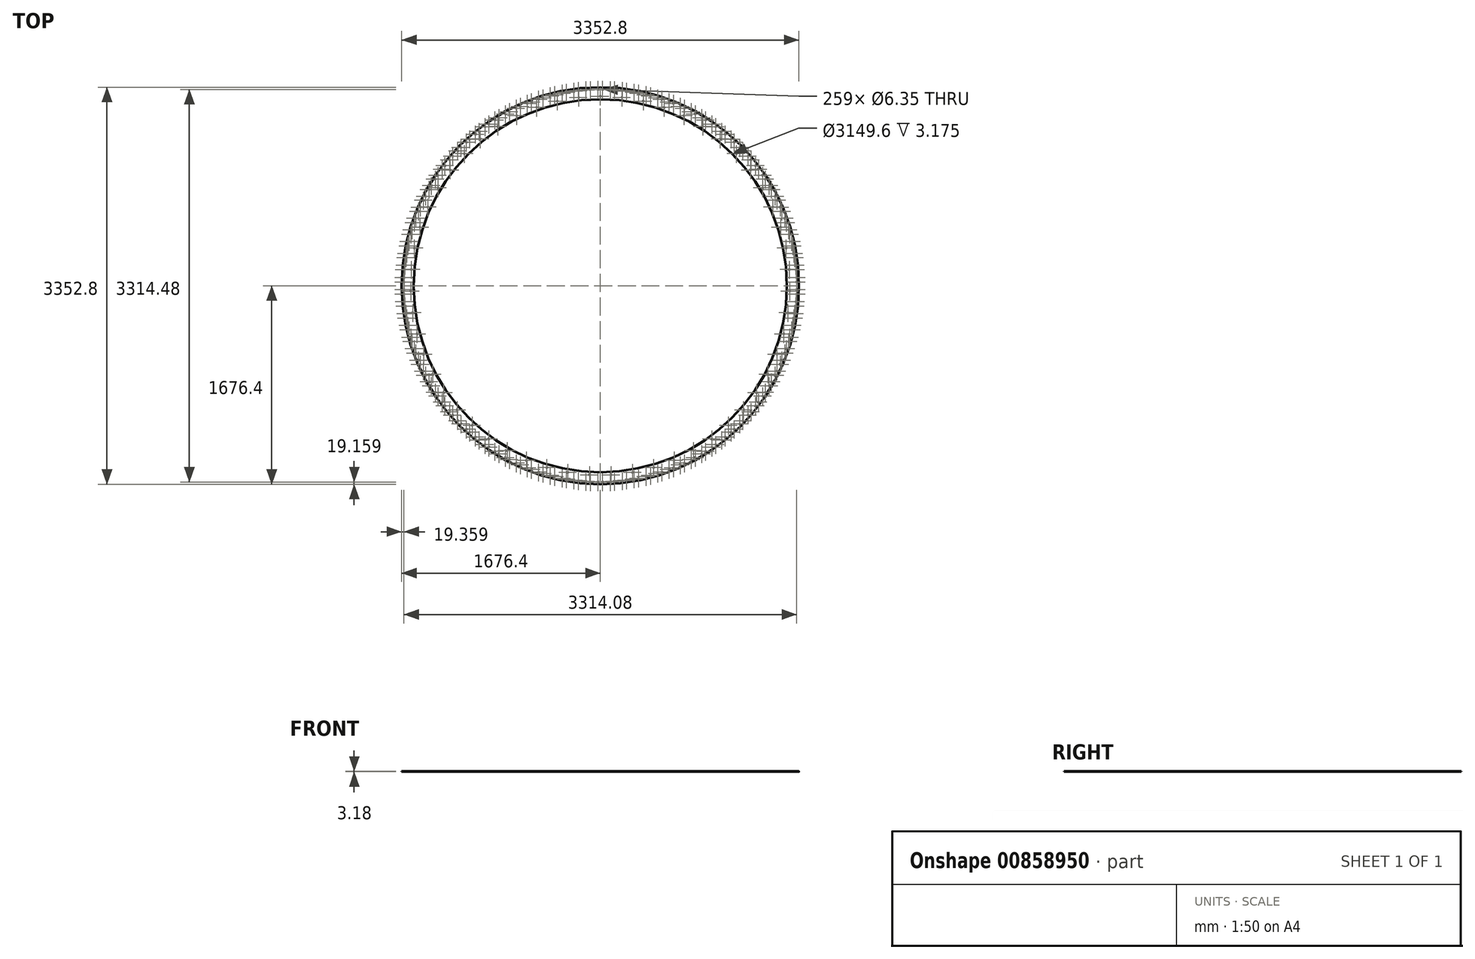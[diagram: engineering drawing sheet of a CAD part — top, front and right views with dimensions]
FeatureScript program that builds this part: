
annotation { "Feature Type Name" : "Feature", "Feature Type Description" : "" }
export const myFeature = defineFeature(function(context is Context, id is Id, definition is map)
    precondition{}
    {
        {
            var Q0;
            Q0=qCreatedBy(makeId("Top.planeOp"),FACE);
            var sketch = newSketch(context, id + "F0", { "sketchPlane" : qUnion([Q0])});
            skCircle(sketch, "E0", {"center": v(0, 0) * mm, "radius": 1676.4 * mm});
            skCircle(sketch, "E1", {"center": v(0, 0) * mm, "radius": 1574.8 * mm});
            skSolve(sketch);
        }
        {
            var Q0;
            Q0=makeQuery(id+"F0.imprint","IMPRINT",FACE,{"disambiguationData":[TD([[makeQuery(id+"F0.imprint","IMPRINT",EDGE,{"derivedFrom":sQuery(id+"F0.wireOp",EDGE,"E0")}),1.0]])]});
            extrude(context, id + "F1", {"entities" : qUnion([Q0]), "depth" : 3.17 * mm, "offsetDistance" : 25.4 * mm});
        }
        {
            var Q0;
            Q0=makeQuery(id+"F1.opExtrude","CAP_FACE",FACE,{"disambiguationData":[OSD([sQuery(id+"F0.wireOp",EDGE,"E0"),sQuery(id+"F0.wireOp",EDGE,"E1")])],"isStart":false});
            var sketch = newSketch(context, id + "F2", { "sketchPlane" : qUnion([Q0])});
            skLineSegment(sketch, "E2", {"start": v(0, 0) * mm, "end": v(0, 1657.35) * mm, "construction": true});
            skCircle(sketch, "E3", {"center": v(0, 0) * mm, "radius": 1657.35 * mm, "construction": true});
            skCircle(sketch, "E4", {"center": v(-19.05, 1657.24) * mm, "radius": 3.18 * mm});
            skCircle(sketch, "E5", {"center": v(19.05, 1657.24) * mm, "radius": 3.18 * mm});
            skCircle(sketch, "E6.1.0", {"center": v(-121.03, 1652.92) * mm, "radius": 3.18 * mm});
            skCircle(sketch, "E6.1.1", {"center": v(-83, 1655.27) * mm, "radius": 3.18 * mm});
            skCircle(sketch, "E6.2.0", {"center": v(-222.56, 1642.34) * mm, "radius": 3.18 * mm});
            skCircle(sketch, "E6.2.1", {"center": v(-184.75, 1647.02) * mm, "radius": 3.18 * mm});
            skCircle(sketch, "E6.3.0", {"center": v(-323.24, 1625.52) * mm, "radius": 3.18 * mm});
            skCircle(sketch, "E6.3.1", {"center": v(-285.8, 1632.52) * mm, "radius": 3.18 * mm});
            skCircle(sketch, "E6.4.0", {"center": v(-422.7, 1602.54) * mm, "radius": 3.18 * mm});
            skCircle(sketch, "E6.4.1", {"center": v(-385.75, 1611.83) * mm, "radius": 3.18 * mm});
            skCircle(sketch, "E6.5.0", {"center": v(-520.55, 1573.48) * mm, "radius": 3.18 * mm});
            skCircle(sketch, "E6.5.1", {"center": v(-484.24, 1585.03) * mm, "radius": 3.18 * mm});
            skCircle(sketch, "E6.6.0", {"center": v(-616.43, 1538.45) * mm, "radius": 3.18 * mm});
            skCircle(sketch, "E6.6.1", {"center": v(-580.9, 1552.21) * mm, "radius": 3.18 * mm});
            skCircle(sketch, "E6.7.0", {"center": v(-709.97, 1497.58) * mm, "radius": 3.18 * mm});
            skCircle(sketch, "E6.7.1", {"center": v(-675.35, 1513.5) * mm, "radius": 3.18 * mm});
            skCircle(sketch, "E6.8.0", {"center": v(-800.81, 1451.04) * mm, "radius": 3.18 * mm});
            skCircle(sketch, "E6.8.1", {"center": v(-767.25, 1469.06) * mm, "radius": 3.18 * mm});
            skCircle(sketch, "E6.9.0", {"center": v(-888.62, 1398.99) * mm, "radius": 3.18 * mm});
            skCircle(sketch, "E6.9.1", {"center": v(-856.23, 1419.04) * mm, "radius": 3.18 * mm});
            skCircle(sketch, "E6.10.0", {"center": v(-973.06, 1341.63) * mm, "radius": 3.18 * mm});
            skCircle(sketch, "E6.10.1", {"center": v(-941.96, 1363.64) * mm, "radius": 3.18 * mm});
            skCircle(sketch, "E6.11.0", {"center": v(-1053.8, 1279.18) * mm, "radius": 3.18 * mm});
            skCircle(sketch, "E6.11.1", {"center": v(-1024.12, 1303.07) * mm, "radius": 3.18 * mm});
            skCircle(sketch, "E6.12.0", {"center": v(-1130.55, 1211.88) * mm, "radius": 3.18 * mm});
            skCircle(sketch, "E6.12.1", {"center": v(-1102.4, 1237.55) * mm, "radius": 3.18 * mm});
            skCircle(sketch, "E6.13.0", {"center": v(-1203.01, 1139.99) * mm, "radius": 3.18 * mm});
            skCircle(sketch, "E6.13.1", {"center": v(-1176.5, 1167.34) * mm, "radius": 3.18 * mm});
            skCircle(sketch, "E6.14.0", {"center": v(-1270.91, 1063.76) * mm, "radius": 3.18 * mm});
            skCircle(sketch, "E6.14.1", {"center": v(-1246.12, 1092.7) * mm, "radius": 3.18 * mm});
            skCircle(sketch, "E6.15.0", {"center": v(-1333.99, 983.5) * mm, "radius": 3.18 * mm});
            skCircle(sketch, "E6.15.1", {"center": v(-1311.03, 1013.91) * mm, "radius": 3.18 * mm});
            skCircle(sketch, "E6.16.0", {"center": v(-1392, 899.52) * mm, "radius": 3.18 * mm});
            skCircle(sketch, "E6.16.1", {"center": v(-1370.96, 931.28) * mm, "radius": 3.18 * mm});
            skCircle(sketch, "E6.17.0", {"center": v(-1444.74, 812.12) * mm, "radius": 3.18 * mm});
            skCircle(sketch, "E6.17.1", {"center": v(-1425.69, 845.12) * mm, "radius": 3.18 * mm});
            skCircle(sketch, "E6.18.0", {"center": v(-1492, 721.64) * mm, "radius": 3.18 * mm});
            skCircle(sketch, "E6.18.1", {"center": v(-1475, 755.75) * mm, "radius": 3.18 * mm});
            skCircle(sketch, "E6.19.0", {"center": v(-1533.59, 628.43) * mm, "radius": 3.18 * mm});
            skCircle(sketch, "E6.19.1", {"center": v(-1518.74, 663.51) * mm, "radius": 3.18 * mm});
            skCircle(sketch, "E6.20.0", {"center": v(-1569.36, 532.83) * mm, "radius": 3.18 * mm});
            skCircle(sketch, "E6.20.1", {"center": v(-1556.7, 568.76) * mm, "radius": 3.18 * mm});
            skCircle(sketch, "E6.21.0", {"center": v(-1599.19, 435.2) * mm, "radius": 3.18 * mm});
            skCircle(sketch, "E6.21.1", {"center": v(-1588.76, 471.85) * mm, "radius": 3.18 * mm});
            skCircle(sketch, "E6.22.0", {"center": v(-1622.95, 335.93) * mm, "radius": 3.18 * mm});
            skCircle(sketch, "E6.22.1", {"center": v(-1614.8, 373.15) * mm, "radius": 3.18 * mm});
            skCircle(sketch, "E6.23.0", {"center": v(-1640.55, 235.38) * mm, "radius": 3.18 * mm});
            skCircle(sketch, "E6.23.1", {"center": v(-1634.7, 273.03) * mm, "radius": 3.18 * mm});
            skCircle(sketch, "E6.24.0", {"center": v(-1651.93, 133.94) * mm, "radius": 3.18 * mm});
            skCircle(sketch, "E6.24.1", {"center": v(-1648.41, 171.88) * mm, "radius": 3.18 * mm});
            skCircle(sketch, "E6.25.0", {"center": v(-1657.04, 32) * mm, "radius": 3.18 * mm});
            skCircle(sketch, "E6.25.1", {"center": v(-1655.87, 70.08) * mm, "radius": 3.18 * mm});
            skCircle(sketch, "E6.26.0", {"center": v(-1655.87, -70.08) * mm, "radius": 3.18 * mm});
            skCircle(sketch, "E6.26.1", {"center": v(-1657.04, -32) * mm, "radius": 3.18 * mm});
            skCircle(sketch, "E6.27.0", {"center": v(-1648.41, -171.88) * mm, "radius": 3.18 * mm});
            skCircle(sketch, "E6.27.1", {"center": v(-1651.93, -133.94) * mm, "radius": 3.18 * mm});
            skCircle(sketch, "E6.28.0", {"center": v(-1634.7, -273.03) * mm, "radius": 3.18 * mm});
            skCircle(sketch, "E6.28.1", {"center": v(-1640.55, -235.38) * mm, "radius": 3.18 * mm});
            skCircle(sketch, "E6.29.0", {"center": v(-1614.8, -373.15) * mm, "radius": 3.18 * mm});
            skCircle(sketch, "E6.29.1", {"center": v(-1622.95, -335.93) * mm, "radius": 3.18 * mm});
            skCircle(sketch, "E6.30.0", {"center": v(-1588.76, -471.85) * mm, "radius": 3.18 * mm});
            skCircle(sketch, "E6.30.1", {"center": v(-1599.19, -435.2) * mm, "radius": 3.18 * mm});
            skCircle(sketch, "E6.31.0", {"center": v(-1556.7, -568.76) * mm, "radius": 3.18 * mm});
            skCircle(sketch, "E6.31.1", {"center": v(-1569.37, -532.82) * mm, "radius": 3.18 * mm});
            skCircle(sketch, "E6.32.0", {"center": v(-1518.74, -663.51) * mm, "radius": 3.18 * mm});
            skCircle(sketch, "E6.32.1", {"center": v(-1533.59, -628.43) * mm, "radius": 3.18 * mm});
            skCircle(sketch, "E6.33.0", {"center": v(-1475, -755.75) * mm, "radius": 3.18 * mm});
            skCircle(sketch, "E6.33.1", {"center": v(-1492, -721.64) * mm, "radius": 3.18 * mm});
            skCircle(sketch, "E6.34.0", {"center": v(-1425.69, -845.12) * mm, "radius": 3.18 * mm});
            skCircle(sketch, "E6.34.1", {"center": v(-1444.74, -812.12) * mm, "radius": 3.18 * mm});
            skCircle(sketch, "E6.35.0", {"center": v(-1370.96, -931.28) * mm, "radius": 3.18 * mm});
            skCircle(sketch, "E6.35.1", {"center": v(-1392, -899.52) * mm, "radius": 3.18 * mm});
            skCircle(sketch, "E6.36.0", {"center": v(-1311.03, -1013.91) * mm, "radius": 3.18 * mm});
            skCircle(sketch, "E6.36.1", {"center": v(-1333.99, -983.5) * mm, "radius": 3.18 * mm});
            skCircle(sketch, "E6.37.0", {"center": v(-1246.12, -1092.7) * mm, "radius": 3.17 * mm});
            skCircle(sketch, "E6.37.1", {"center": v(-1270.91, -1063.76) * mm, "radius": 3.17 * mm});
            skCircle(sketch, "E6.38.0", {"center": v(-1176.5, -1167.34) * mm, "radius": 3.18 * mm});
            skCircle(sketch, "E6.38.1", {"center": v(-1203.01, -1139.99) * mm, "radius": 3.18 * mm});
            skCircle(sketch, "E6.39.0", {"center": v(-1102.4, -1237.55) * mm, "radius": 3.18 * mm});
            skCircle(sketch, "E6.39.1", {"center": v(-1130.55, -1211.88) * mm, "radius": 3.18 * mm});
            skCircle(sketch, "E6.40.0", {"center": v(-1024.12, -1303.07) * mm, "radius": 3.18 * mm});
            skCircle(sketch, "E6.40.1", {"center": v(-1053.8, -1279.18) * mm, "radius": 3.18 * mm});
            skCircle(sketch, "E6.41.0", {"center": v(-941.96, -1363.64) * mm, "radius": 3.18 * mm});
            skCircle(sketch, "E6.41.1", {"center": v(-973.06, -1341.63) * mm, "radius": 3.18 * mm});
            skCircle(sketch, "E6.42.0", {"center": v(-856.23, -1419.04) * mm, "radius": 3.18 * mm});
            skCircle(sketch, "E6.42.1", {"center": v(-888.62, -1398.99) * mm, "radius": 3.18 * mm});
            skCircle(sketch, "E6.43.0", {"center": v(-767.25, -1469.06) * mm, "radius": 3.18 * mm});
            skCircle(sketch, "E6.43.1", {"center": v(-800.81, -1451.04) * mm, "radius": 3.18 * mm});
            skCircle(sketch, "E6.44.0", {"center": v(-675.35, -1513.5) * mm, "radius": 3.18 * mm});
            skCircle(sketch, "E6.44.1", {"center": v(-709.97, -1497.58) * mm, "radius": 3.18 * mm});
            skCircle(sketch, "E6.45.0", {"center": v(-580.9, -1552.21) * mm, "radius": 3.18 * mm});
            skCircle(sketch, "E6.45.1", {"center": v(-616.43, -1538.45) * mm, "radius": 3.18 * mm});
            skCircle(sketch, "E6.46.0", {"center": v(-484.24, -1585.03) * mm, "radius": 3.18 * mm});
            skCircle(sketch, "E6.46.1", {"center": v(-520.55, -1573.48) * mm, "radius": 3.18 * mm});
            skCircle(sketch, "E6.47.0", {"center": v(-385.75, -1611.83) * mm, "radius": 3.18 * mm});
            skCircle(sketch, "E6.47.1", {"center": v(-422.7, -1602.54) * mm, "radius": 3.18 * mm});
            skCircle(sketch, "E6.48.0", {"center": v(-285.8, -1632.52) * mm, "radius": 3.18 * mm});
            skCircle(sketch, "E6.48.1", {"center": v(-323.24, -1625.52) * mm, "radius": 3.18 * mm});
            skCircle(sketch, "E6.49.0", {"center": v(-184.75, -1647.02) * mm, "radius": 3.18 * mm});
            skCircle(sketch, "E6.49.1", {"center": v(-222.56, -1642.34) * mm, "radius": 3.18 * mm});
            skCircle(sketch, "E6.50.0", {"center": v(-83, -1655.27) * mm, "radius": 3.18 * mm});
            skCircle(sketch, "E6.50.1", {"center": v(-121.04, -1652.92) * mm, "radius": 3.18 * mm});
            skCircle(sketch, "E6.51.0", {"center": v(19.05, -1657.24) * mm, "radius": 3.18 * mm});
            skCircle(sketch, "E6.51.1", {"center": v(-19.05, -1657.24) * mm, "radius": 3.18 * mm});
            skCircle(sketch, "E6.52.0", {"center": v(121.03, -1652.92) * mm, "radius": 3.18 * mm});
            skCircle(sketch, "E6.52.1", {"center": v(83, -1655.27) * mm, "radius": 3.18 * mm});
            skCircle(sketch, "E6.53.0", {"center": v(222.56, -1642.34) * mm, "radius": 3.18 * mm});
            skCircle(sketch, "E6.53.1", {"center": v(184.75, -1647.02) * mm, "radius": 3.18 * mm});
            skCircle(sketch, "E6.54.0", {"center": v(323.24, -1625.52) * mm, "radius": 3.18 * mm});
            skCircle(sketch, "E6.54.1", {"center": v(285.8, -1632.52) * mm, "radius": 3.18 * mm});
            skCircle(sketch, "E6.55.0", {"center": v(422.7, -1602.54) * mm, "radius": 3.18 * mm});
            skCircle(sketch, "E6.55.1", {"center": v(385.75, -1611.83) * mm, "radius": 3.18 * mm});
            skCircle(sketch, "E6.56.0", {"center": v(520.55, -1573.48) * mm, "radius": 3.18 * mm});
            skCircle(sketch, "E6.56.1", {"center": v(484.24, -1585.03) * mm, "radius": 3.18 * mm});
            skCircle(sketch, "E6.57.0", {"center": v(616.43, -1538.45) * mm, "radius": 3.18 * mm});
            skCircle(sketch, "E6.57.1", {"center": v(580.9, -1552.21) * mm, "radius": 3.18 * mm});
            skCircle(sketch, "E6.58.0", {"center": v(709.97, -1497.58) * mm, "radius": 3.18 * mm});
            skCircle(sketch, "E6.58.1", {"center": v(675.35, -1513.5) * mm, "radius": 3.18 * mm});
            skCircle(sketch, "E6.59.0", {"center": v(800.81, -1451.04) * mm, "radius": 3.18 * mm});
            skCircle(sketch, "E6.59.1", {"center": v(767.25, -1469.06) * mm, "radius": 3.18 * mm});
            skCircle(sketch, "E6.60.0", {"center": v(888.62, -1398.99) * mm, "radius": 3.18 * mm});
            skCircle(sketch, "E6.60.1", {"center": v(856.23, -1419.04) * mm, "radius": 3.18 * mm});
            skCircle(sketch, "E6.61.0", {"center": v(973.06, -1341.63) * mm, "radius": 3.18 * mm});
            skCircle(sketch, "E6.61.1", {"center": v(941.96, -1363.64) * mm, "radius": 3.18 * mm});
            skCircle(sketch, "E6.62.0", {"center": v(1053.8, -1279.18) * mm, "radius": 3.18 * mm});
            skCircle(sketch, "E6.62.1", {"center": v(1024.12, -1303.07) * mm, "radius": 3.18 * mm});
            skCircle(sketch, "E6.63.0", {"center": v(1130.55, -1211.88) * mm, "radius": 3.18 * mm});
            skCircle(sketch, "E6.63.1", {"center": v(1102.4, -1237.55) * mm, "radius": 3.18 * mm});
            skCircle(sketch, "E6.64.0", {"center": v(1203.01, -1139.99) * mm, "radius": 3.18 * mm});
            skCircle(sketch, "E6.64.1", {"center": v(1176.5, -1167.34) * mm, "radius": 3.18 * mm});
            skCircle(sketch, "E6.65.0", {"center": v(1270.91, -1063.76) * mm, "radius": 3.18 * mm});
            skCircle(sketch, "E6.65.1", {"center": v(1246.12, -1092.7) * mm, "radius": 3.18 * mm});
            skCircle(sketch, "E6.66.0", {"center": v(1333.99, -983.5) * mm, "radius": 3.18 * mm});
            skCircle(sketch, "E6.66.1", {"center": v(1311.03, -1013.91) * mm, "radius": 3.18 * mm});
            skCircle(sketch, "E6.67.0", {"center": v(1392, -899.52) * mm, "radius": 3.18 * mm});
            skCircle(sketch, "E6.67.1", {"center": v(1370.96, -931.28) * mm, "radius": 3.18 * mm});
            skCircle(sketch, "E6.68.0", {"center": v(1444.74, -812.12) * mm, "radius": 3.18 * mm});
            skCircle(sketch, "E6.68.1", {"center": v(1425.69, -845.12) * mm, "radius": 3.18 * mm});
            skCircle(sketch, "E6.69.0", {"center": v(1492, -721.64) * mm, "radius": 3.18 * mm});
            skCircle(sketch, "E6.69.1", {"center": v(1475, -755.75) * mm, "radius": 3.18 * mm});
            skCircle(sketch, "E6.70.0", {"center": v(1533.59, -628.43) * mm, "radius": 3.18 * mm});
            skCircle(sketch, "E6.70.1", {"center": v(1518.74, -663.51) * mm, "radius": 3.18 * mm});
            skCircle(sketch, "E6.71.0", {"center": v(1569.36, -532.83) * mm, "radius": 3.18 * mm});
            skCircle(sketch, "E6.71.1", {"center": v(1556.7, -568.76) * mm, "radius": 3.18 * mm});
            skCircle(sketch, "E6.72.0", {"center": v(1599.19, -435.2) * mm, "radius": 3.18 * mm});
            skCircle(sketch, "E6.72.1", {"center": v(1588.76, -471.85) * mm, "radius": 3.18 * mm});
            skCircle(sketch, "E6.73.0", {"center": v(1622.95, -335.93) * mm, "radius": 3.18 * mm});
            skCircle(sketch, "E6.73.1", {"center": v(1614.8, -373.15) * mm, "radius": 3.18 * mm});
            skCircle(sketch, "E6.74.0", {"center": v(1640.55, -235.38) * mm, "radius": 3.18 * mm});
            skCircle(sketch, "E6.74.1", {"center": v(1634.7, -273.03) * mm, "radius": 3.18 * mm});
            skCircle(sketch, "E6.75.0", {"center": v(1651.93, -133.94) * mm, "radius": 3.18 * mm});
            skCircle(sketch, "E6.75.1", {"center": v(1648.41, -171.88) * mm, "radius": 3.18 * mm});
            skCircle(sketch, "E6.76.0", {"center": v(1657.04, -32) * mm, "radius": 3.18 * mm});
            skCircle(sketch, "E6.76.1", {"center": v(1655.87, -70.08) * mm, "radius": 3.18 * mm});
            skCircle(sketch, "E6.77.0", {"center": v(1655.87, 70.08) * mm, "radius": 3.18 * mm});
            skCircle(sketch, "E6.77.1", {"center": v(1657.04, 32) * mm, "radius": 3.18 * mm});
            skCircle(sketch, "E6.78.0", {"center": v(1648.41, 171.88) * mm, "radius": 3.18 * mm});
            skCircle(sketch, "E6.78.1", {"center": v(1651.93, 133.94) * mm, "radius": 3.18 * mm});
            skCircle(sketch, "E6.79.0", {"center": v(1634.7, 273.03) * mm, "radius": 3.18 * mm});
            skCircle(sketch, "E6.79.1", {"center": v(1640.55, 235.38) * mm, "radius": 3.18 * mm});
            skCircle(sketch, "E6.80.0", {"center": v(1614.8, 373.15) * mm, "radius": 3.18 * mm});
            skCircle(sketch, "E6.80.1", {"center": v(1622.95, 335.93) * mm, "radius": 3.18 * mm});
            skCircle(sketch, "E6.81.0", {"center": v(1588.76, 471.85) * mm, "radius": 3.18 * mm});
            skCircle(sketch, "E6.81.1", {"center": v(1599.19, 435.2) * mm, "radius": 3.18 * mm});
            skCircle(sketch, "E6.82.0", {"center": v(1556.7, 568.76) * mm, "radius": 3.18 * mm});
            skCircle(sketch, "E6.82.1", {"center": v(1569.37, 532.82) * mm, "radius": 3.18 * mm});
            skCircle(sketch, "E6.83.0", {"center": v(1518.74, 663.51) * mm, "radius": 3.18 * mm});
            skCircle(sketch, "E6.83.1", {"center": v(1533.59, 628.43) * mm, "radius": 3.18 * mm});
            skCircle(sketch, "E6.84.0", {"center": v(1475, 755.75) * mm, "radius": 3.18 * mm});
            skCircle(sketch, "E6.84.1", {"center": v(1492, 721.64) * mm, "radius": 3.18 * mm});
            skCircle(sketch, "E6.85.0", {"center": v(1425.69, 845.12) * mm, "radius": 3.18 * mm});
            skCircle(sketch, "E6.85.1", {"center": v(1444.74, 812.12) * mm, "radius": 3.18 * mm});
            skCircle(sketch, "E6.86.0", {"center": v(1370.96, 931.28) * mm, "radius": 3.18 * mm});
            skCircle(sketch, "E6.86.1", {"center": v(1392, 899.52) * mm, "radius": 3.18 * mm});
            skCircle(sketch, "E6.87.0", {"center": v(1311.03, 1013.91) * mm, "radius": 3.18 * mm});
            skCircle(sketch, "E6.87.1", {"center": v(1333.99, 983.5) * mm, "radius": 3.18 * mm});
            skCircle(sketch, "E6.88.0", {"center": v(1246.12, 1092.7) * mm, "radius": 3.18 * mm});
            skCircle(sketch, "E6.88.1", {"center": v(1270.91, 1063.76) * mm, "radius": 3.18 * mm});
            skCircle(sketch, "E6.89.0", {"center": v(1176.5, 1167.34) * mm, "radius": 3.18 * mm});
            skCircle(sketch, "E6.89.1", {"center": v(1203.01, 1139.99) * mm, "radius": 3.18 * mm});
            skCircle(sketch, "E6.90.0", {"center": v(1102.4, 1237.55) * mm, "radius": 3.18 * mm});
            skCircle(sketch, "E6.90.1", {"center": v(1130.55, 1211.88) * mm, "radius": 3.18 * mm});
            skCircle(sketch, "E6.91.0", {"center": v(1024.12, 1303.07) * mm, "radius": 3.18 * mm});
            skCircle(sketch, "E6.91.1", {"center": v(1053.8, 1279.18) * mm, "radius": 3.18 * mm});
            skCircle(sketch, "E6.92.0", {"center": v(941.96, 1363.64) * mm, "radius": 3.18 * mm});
            skCircle(sketch, "E6.92.1", {"center": v(973.06, 1341.63) * mm, "radius": 3.18 * mm});
            skCircle(sketch, "E6.93.0", {"center": v(856.23, 1419.04) * mm, "radius": 3.18 * mm});
            skCircle(sketch, "E6.93.1", {"center": v(888.62, 1398.99) * mm, "radius": 3.18 * mm});
            skCircle(sketch, "E6.94.0", {"center": v(767.25, 1469.06) * mm, "radius": 3.18 * mm});
            skCircle(sketch, "E6.94.1", {"center": v(800.81, 1451.04) * mm, "radius": 3.18 * mm});
            skCircle(sketch, "E6.95.0", {"center": v(675.35, 1513.5) * mm, "radius": 3.18 * mm});
            skCircle(sketch, "E6.95.1", {"center": v(709.97, 1497.58) * mm, "radius": 3.18 * mm});
            skCircle(sketch, "E6.96.0", {"center": v(580.9, 1552.21) * mm, "radius": 3.18 * mm});
            skCircle(sketch, "E6.96.1", {"center": v(616.43, 1538.45) * mm, "radius": 3.18 * mm});
            skCircle(sketch, "E6.97.0", {"center": v(484.24, 1585.03) * mm, "radius": 3.18 * mm});
            skCircle(sketch, "E6.97.1", {"center": v(520.55, 1573.48) * mm, "radius": 3.18 * mm});
            skCircle(sketch, "E6.98.0", {"center": v(385.75, 1611.83) * mm, "radius": 3.18 * mm});
            skCircle(sketch, "E6.98.1", {"center": v(422.7, 1602.54) * mm, "radius": 3.18 * mm});
            skCircle(sketch, "E6.99.0", {"center": v(285.8, 1632.52) * mm, "radius": 3.18 * mm});
            skCircle(sketch, "E6.99.1", {"center": v(323.24, 1625.52) * mm, "radius": 3.18 * mm});
            skCircle(sketch, "E6.100.0", {"center": v(184.75, 1647.02) * mm, "radius": 3.18 * mm});
            skCircle(sketch, "E6.100.1", {"center": v(222.56, 1642.34) * mm, "radius": 3.18 * mm});
            skCircle(sketch, "E6.101.0", {"center": v(83, 1655.27) * mm, "radius": 3.18 * mm});
            skCircle(sketch, "E6.101.1", {"center": v(121.04, 1652.92) * mm, "radius": 3.18 * mm});
            skSolve(sketch);
        }
        {
            var Q0;
            Q0 = qSketchRegion(id + "F2", true);
            extrude(context, id + "F3", {"entities" : qUnion([Q0]), "operationType" : NewBodyOperationType.REMOVE, "oppositeDirection" : true, "depth" : 25.4 * mm, "offsetDistance" : 25.4 * mm});
        }
        {
            var Q0;
            Q0=makeQuery(id+"F1.opExtrude","CAP_FACE",FACE,{"disambiguationData":[OSD([sQuery(id+"F0.wireOp",EDGE,"E0"),sQuery(id+"F0.wireOp",EDGE,"E1")])],"isStart":false});
            var sketch = newSketch(context, id + "F4", { "sketchPlane" : qUnion([Q0])});
            skLineSegment(sketch, "E7", {"start": v(0, 0) * mm, "end": v(0, 1600.2) * mm, "construction": true});
            skCircle(sketch, "E8", {"center": v(0, 1600.2) * mm, "radius": 3.18 * mm});
            skCircle(sketch, "E9.1.0", {"center": v(-182.4, 1589.77) * mm, "radius": 3.18 * mm});
            skCircle(sketch, "E9.2.0", {"center": v(-362.44, 1558.61) * mm, "radius": 3.18 * mm});
            skCircle(sketch, "E9.3.0", {"center": v(-537.75, 1507.14) * mm, "radius": 3.18 * mm});
            skCircle(sketch, "E9.4.0", {"center": v(-706.04, 1436.02) * mm, "radius": 3.18 * mm});
            skCircle(sketch, "E9.5.0", {"center": v(-865.13, 1346.17) * mm, "radius": 3.18 * mm});
            skCircle(sketch, "E9.6.0", {"center": v(-1012.95, 1238.78) * mm, "radius": 3.18 * mm});
            skCircle(sketch, "E9.7.0", {"center": v(-1147.55, 1115.24) * mm, "radius": 3.18 * mm});
            skCircle(sketch, "E9.8.0", {"center": v(-1267.2, 977.16) * mm, "radius": 3.18 * mm});
            skCircle(sketch, "E9.9.0", {"center": v(-1370.33, 826.34) * mm, "radius": 3.18 * mm});
            skCircle(sketch, "E9.10.0", {"center": v(-1455.6, 664.75) * mm, "radius": 3.18 * mm});
            skCircle(sketch, "E9.11.0", {"center": v(-1521.88, 494.49) * mm, "radius": 3.18 * mm});
            skCircle(sketch, "E9.12.0", {"center": v(-1568.33, 317.78) * mm, "radius": 3.18 * mm});
            skCircle(sketch, "E9.13.0", {"center": v(-1594.33, 136.94) * mm, "radius": 3.18 * mm});
            skCircle(sketch, "E9.14.0", {"center": v(-1599.55, -45.7) * mm, "radius": 3.18 * mm});
            skCircle(sketch, "E9.15.0", {"center": v(-1583.91, -227.73) * mm, "radius": 3.18 * mm});
            skCircle(sketch, "E9.16.0", {"center": v(-1547.63, -406.8) * mm, "radius": 3.18 * mm});
            skCircle(sketch, "E9.17.0", {"center": v(-1491.17, -580.56) * mm, "radius": 3.18 * mm});
            skCircle(sketch, "E9.18.0", {"center": v(-1415.27, -746.76) * mm, "radius": 3.18 * mm});
            skCircle(sketch, "E9.19.0", {"center": v(-1320.92, -903.22) * mm, "radius": 3.18 * mm});
            skCircle(sketch, "E9.20.0", {"center": v(-1209.35, -1047.9) * mm, "radius": 3.18 * mm});
            skCircle(sketch, "E9.21.0", {"center": v(-1082.02, -1178.93) * mm, "radius": 3.18 * mm});
            skCircle(sketch, "E9.22.0", {"center": v(-940.57, -1294.59) * mm, "radius": 3.18 * mm});
            skCircle(sketch, "E9.23.0", {"center": v(-786.87, -1393.37) * mm, "radius": 3.18 * mm});
            skCircle(sketch, "E9.24.0", {"center": v(-622.91, -1473.98) * mm, "radius": 3.18 * mm});
            skCircle(sketch, "E9.25.0", {"center": v(-450.83, -1535.38) * mm, "radius": 3.18 * mm});
            skCircle(sketch, "E9.26.0", {"center": v(-272.87, -1576.76) * mm, "radius": 3.18 * mm});
            skCircle(sketch, "E9.27.0", {"center": v(-91.35, -1597.6) * mm, "radius": 3.18 * mm});
            skCircle(sketch, "E9.28.0", {"center": v(91.35, -1597.6) * mm, "radius": 3.18 * mm});
            skCircle(sketch, "E9.29.0", {"center": v(272.87, -1576.76) * mm, "radius": 3.18 * mm});
            skCircle(sketch, "E9.30.0", {"center": v(450.83, -1535.38) * mm, "radius": 3.18 * mm});
            skCircle(sketch, "E9.31.0", {"center": v(622.91, -1473.98) * mm, "radius": 3.18 * mm});
            skCircle(sketch, "E9.32.0", {"center": v(786.87, -1393.37) * mm, "radius": 3.18 * mm});
            skCircle(sketch, "E9.33.0", {"center": v(940.57, -1294.59) * mm, "radius": 3.18 * mm});
            skCircle(sketch, "E9.34.0", {"center": v(1082.02, -1178.93) * mm, "radius": 3.18 * mm});
            skCircle(sketch, "E9.35.0", {"center": v(1209.35, -1047.9) * mm, "radius": 3.18 * mm});
            skCircle(sketch, "E9.36.0", {"center": v(1320.92, -903.22) * mm, "radius": 3.18 * mm});
            skCircle(sketch, "E9.37.0", {"center": v(1415.27, -746.76) * mm, "radius": 3.18 * mm});
            skCircle(sketch, "E9.38.0", {"center": v(1491.17, -580.56) * mm, "radius": 3.18 * mm});
            skCircle(sketch, "E9.39.0", {"center": v(1547.63, -406.8) * mm, "radius": 3.18 * mm});
            skCircle(sketch, "E9.40.0", {"center": v(1583.91, -227.73) * mm, "radius": 3.18 * mm});
            skCircle(sketch, "E9.41.0", {"center": v(1599.55, -45.7) * mm, "radius": 3.18 * mm});
            skCircle(sketch, "E9.42.0", {"center": v(1594.33, 136.94) * mm, "radius": 3.18 * mm});
            skCircle(sketch, "E9.43.0", {"center": v(1568.33, 317.78) * mm, "radius": 3.18 * mm});
            skCircle(sketch, "E9.44.0", {"center": v(1521.88, 494.49) * mm, "radius": 3.18 * mm});
            skCircle(sketch, "E9.45.0", {"center": v(1455.6, 664.75) * mm, "radius": 3.18 * mm});
            skCircle(sketch, "E9.46.0", {"center": v(1370.33, 826.34) * mm, "radius": 3.18 * mm});
            skCircle(sketch, "E9.47.0", {"center": v(1267.2, 977.16) * mm, "radius": 3.18 * mm});
            skCircle(sketch, "E9.48.0", {"center": v(1147.55, 1115.24) * mm, "radius": 3.18 * mm});
            skCircle(sketch, "E9.49.0", {"center": v(1012.95, 1238.78) * mm, "radius": 3.18 * mm});
            skCircle(sketch, "E9.50.0", {"center": v(865.13, 1346.17) * mm, "radius": 3.18 * mm});
            skCircle(sketch, "E9.51.0", {"center": v(706.04, 1436.02) * mm, "radius": 3.18 * mm});
            skCircle(sketch, "E9.52.0", {"center": v(537.75, 1507.14) * mm, "radius": 3.18 * mm});
            skCircle(sketch, "E9.53.0", {"center": v(362.44, 1558.61) * mm, "radius": 3.18 * mm});
            skCircle(sketch, "E9.54.0", {"center": v(182.4, 1589.77) * mm, "radius": 3.18 * mm});
            skPoint(sketch, "E9.center", {"position": v(0, 0) * mm});
            skSolve(sketch);
        }
        {
            var Q0;
            Q0 = qSketchRegion(id + "F4", true);
            extrude(context, id + "F5", {"entities" : qUnion([Q0]), "operationType" : NewBodyOperationType.REMOVE, "oppositeDirection" : true, "depth" : 25.4 * mm, "offsetDistance" : 25.4 * mm});
        }
    });
